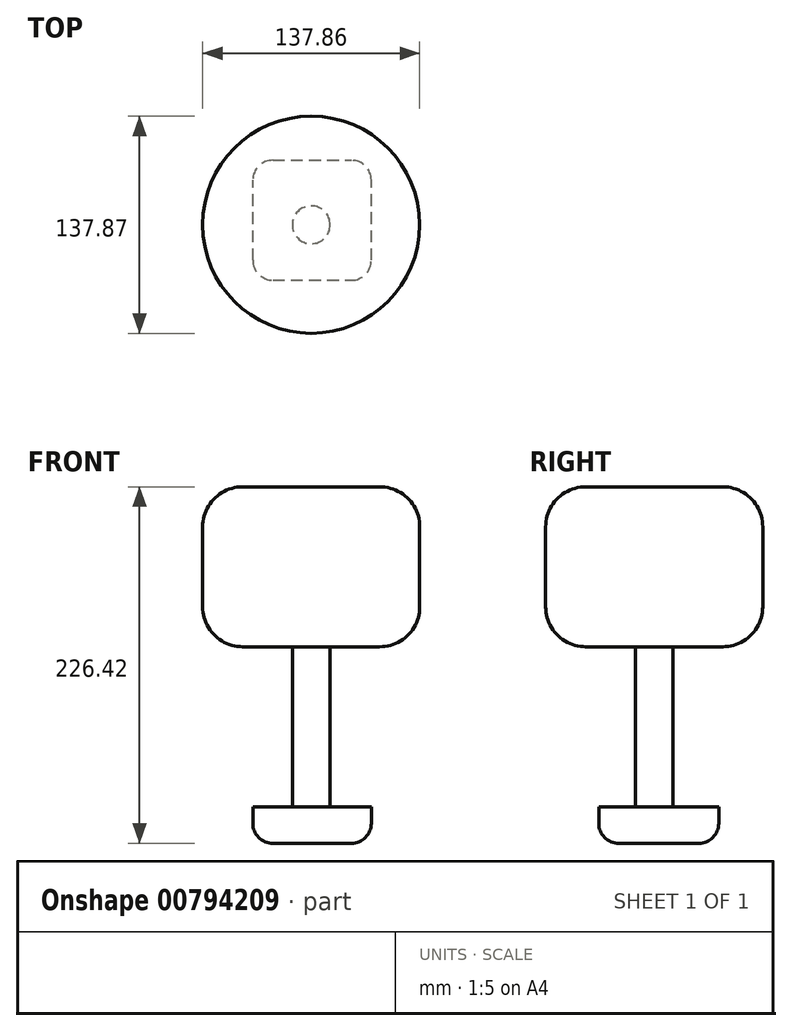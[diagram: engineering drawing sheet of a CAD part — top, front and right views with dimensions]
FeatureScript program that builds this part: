
annotation { "Feature Type Name" : "Feature", "Feature Type Description" : "" }
export const myFeature = defineFeature(function(context is Context, id is Id, definition is map)
    precondition{}
    {
        {
            var Q0;
            Q0=qCreatedBy(makeId("Front.planeOp"),FACE);
            var sketch = newSketch(context, id + "F0", { "sketchPlane" : qUnion([Q0])});
            skLineSegment(sketch, "E0.bottom", {"start": v(-37.07, -54.97) * mm, "end": v(38.19, -54.97) * mm});
            skLineSegment(sketch, "E0.top", {"start": v(-37.07, -31.75) * mm, "end": v(38.19, -31.75) * mm});
            skLineSegment(sketch, "E0.left", {"start": v(-37.07, -54.97) * mm, "end": v(-37.07, -31.75) * mm});
            skLineSegment(sketch, "E0.right", {"start": v(38.19, -54.97) * mm, "end": v(38.19, -31.75) * mm});
            skSolve(sketch);
        }
        {
            var Q0;
            Q0=makeQuery(id+"F0.imprint","IMPRINT",FACE,{"disambiguationData":[TD([[makeQuery(id+"F0.imprint","IMPRINT",EDGE,{"derivedFrom":sQuery(id+"F0.wireOp",EDGE,"E0.bottom")}),1.0]])]});
            extrude(context, id + "F1", {"entities" : qUnion([Q0]), "depth" : 76.2 * mm, "offsetDistance" : 25.4 * mm});
        }
        {
            var Q0;
            Q0=makeQuery(id+"F1.opExtrude","SWEPT_FACE",FACE,{"disambiguationData":[OSD([sQuery(id+"F0.wireOp",EDGE,"E0.top")])]});
            var sketch = newSketch(context, id + "F2", { "sketchPlane" : qUnion([Q0])});
            skCircle(sketch, "E1", {"center": v(0, -40.98) * mm, "radius": 12.02 * mm});
            skSolve(sketch);
        }
        {
            var Q0;
            Q0=makeQuery(id+"F2.imprint","IMPRINT",FACE,{"disambiguationData":[TD([[makeQuery(id+"F2.imprint","IMPRINT",EDGE,{"derivedFrom":sQuery(id+"F2.wireOp",EDGE,"E1")}),1.0]])]});
            extrude(context, id + "F3", {"entities" : qUnion([Q0]), "operationType" : NewBodyOperationType.ADD, "depth" : 101.6 * mm, "offsetDistance" : 25.4 * mm});
        }
        {
            var Q0;
            Q0=makeQuery(id+"F3.opExtrude","CAP_FACE",FACE,{"disambiguationData":[OSD([sQuery(id+"F2.wireOp",EDGE,"E1")])],"isStart":false});
            var sketch = newSketch(context, id + "F4", { "sketchPlane" : qUnion([Q0])});
            skCircle(sketch, "E2", {"center": v(0, -40.98) * mm, "radius": 68.93 * mm});
            skSolve(sketch);
        }
        {
            var Q0;
            Q0 = qSketchRegion(id + "F4", true);
            extrude(context, id + "F5", {"entities" : qUnion([Q0]), "operationType" : NewBodyOperationType.ADD, "depth" : 101.6 * mm, "offsetDistance" : 25.4 * mm});
        }
        {
            var Q0;
            Q0=makeQuery(id+"F5.opExtrude","CAP_EDGE",EDGE,{"disambiguationData":[OSD([sQuery(id+"F4.wireOp",EDGE,"E2")])],"isStart":false});
            var Q1;
            Q1=makeQuery(id+"F5.opExtrude","CAP_EDGE",EDGE,{"disambiguationData":[OSD([sQuery(id+"F4.wireOp",EDGE,"E2")])],"isStart":true});
            fillet(context, id + "F6", {"entities" : qUnion([Q0, Q1]), "radius" : 25.4 * mm, "tangentPropagation" : true, "allowEdgeOverflow" : false});
        }
        {
            var Q0;
            Q0=makeQuery(id+"F1.opExtrude","CAP_EDGE",EDGE,{"disambiguationData":[OSD([sQuery(id+"F0.wireOp",EDGE,"E0.right")])],"isStart":false});
            var Q1;
            Q1=makeQuery(id+"F1.opExtrude","CAP_EDGE",EDGE,{"disambiguationData":[OSD([sQuery(id+"F0.wireOp",EDGE,"E0.right")])],"isStart":true});
            var Q2;
            Q2=makeQuery(id+"F1.opExtrude","CAP_EDGE",EDGE,{"disambiguationData":[OSD([sQuery(id+"F0.wireOp",EDGE,"E0.left")])],"isStart":false});
            var Q3;
            Q3=makeQuery(id+"F1.opExtrude","CAP_EDGE",EDGE,{"disambiguationData":[OSD([sQuery(id+"F0.wireOp",EDGE,"E0.bottom")])],"isStart":false});
            var Q4;
            Q4=makeQuery(id+"F1.opExtrude","SWEPT_EDGE",EDGE,{"disambiguationData":[OSD([sQuery(id+"F0.wireOp",EDGE,"E0.bottom"),sQuery(id+"F0.wireOp",EDGE,"E0.right")])]});
            var Q5;
            Q5=makeQuery(id+"F1.opExtrude","CAP_EDGE",EDGE,{"disambiguationData":[OSD([sQuery(id+"F0.wireOp",EDGE,"E0.bottom")])],"isStart":true});
            var Q6;
            Q6=makeQuery(id+"F1.opExtrude","SWEPT_EDGE",EDGE,{"disambiguationData":[OSD([sQuery(id+"F0.wireOp",EDGE,"E0.bottom"),sQuery(id+"F0.wireOp",EDGE,"E0.left")])]});
            var Q7;
            Q7=makeQuery(id+"F1.opExtrude","CAP_EDGE",EDGE,{"disambiguationData":[OSD([sQuery(id+"F0.wireOp",EDGE,"E0.left")])],"isStart":true});
            fillet(context, id + "F7", {"entities" : qUnion([Q0, Q1, Q2, Q3, Q4, Q5, Q6, Q7]), "radius" : 12.7 * mm, "tangentPropagation" : true, "allowEdgeOverflow" : false});
        }
    });
